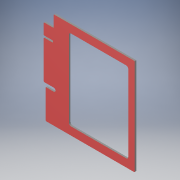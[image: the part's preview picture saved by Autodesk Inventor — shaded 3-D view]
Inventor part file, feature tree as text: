
AUTODESK INVENTOR PART (.ipt)
format: ipt  version: 2018 (Build 220112000, 112)  size: 216,064 bytes
history: native  units: in
note: dims shown in document units (in); Inventor stores cm internally (conversion verified against a paired STEP export)
features: extrude x2, chamfer x1, fillet x1, sketch x1, projected_geometry x1
ambient origin geometry x8: Origin, YZ Plane, XZ Plane, XY Plane, X Axis, Y Axis, Z Axis, Center Point
bodies: Solid1 (feature_tree)
feature tree (6):
  extrude  "Extrusion1"  Depth=3.7717in
  chamfer  "Chamfer1"  Distance=0.3937in
  fillet  "Fillet1"  Radius=0.063in
  extrude  "Extrusion6"  Depth=0.3937in
  sketch  "Sketch16"  dims[d0=2.0197in d1=3.7717in d3=0.3937in d4=0.063in d5=0.0in d20=3.7795in d21=3.7795in d22=0.0039in d23=0.0039in d24=0.0787in d25=0.0039in d28=0.4429in d29=2.2047in d31=0.374in d32=1.2008in d34=0.1378in d35=0.4783in d36=1.5413in d37=0.5709in d38=0.0453in d39=0.0709in d40=2.7559in d42=0.0709in d43=1.9685in d45=0.0709in d48=0.0787in d49=0.1339in d50=0.0748in d51=0.3307in d52=0.9449in d53=0.0197in d54=0.0787in d55=45.0deg d56=0.0197in d145=3.1496in d146=0.9843in d147=3.3071in d148=0.0787in d149=0.3937in d150=0.0in]
  projected_geometry  "Projected Loop5"
